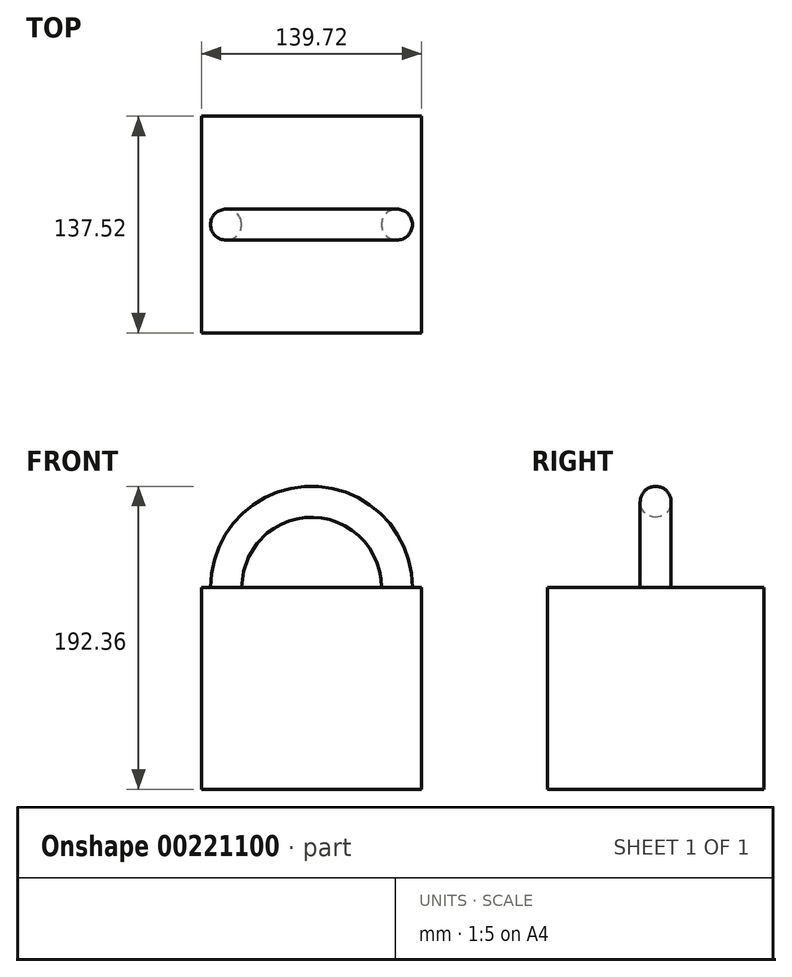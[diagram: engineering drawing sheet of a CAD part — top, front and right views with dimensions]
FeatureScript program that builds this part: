
annotation { "Feature Type Name" : "Feature", "Feature Type Description" : "" }
export const myFeature = defineFeature(function(context is Context, id is Id, definition is map)
    precondition{}
    {
        {
            var Q0;
            Q0=qCreatedBy(makeId("Top.planeOp"),FACE);
            var sketch = newSketch(context, id + "F0", { "sketchPlane" : qUnion([Q0])});
            skLineSegment(sketch, "E0.bottom", {"start": v(69.86, -68.76) * mm, "end": v(-69.86, -68.76) * mm});
            skLineSegment(sketch, "E0.top", {"start": v(69.86, 68.76) * mm, "end": v(-69.86, 68.76) * mm});
            skLineSegment(sketch, "E0.left", {"start": v(69.86, -68.76) * mm, "end": v(69.86, 68.76) * mm});
            skLineSegment(sketch, "E0.right", {"start": v(-69.86, -68.76) * mm, "end": v(-69.86, 68.76) * mm});
            skPoint(sketch, "E0.middle", {"position": v(0, 0) * mm});
            skLineSegment(sketch, "E1", {"start": v(0, 68.76) * mm, "end": v(0, -68.76) * mm});
            skSolve(sketch);
        }
        {
            var Q0;
            Q0=qCreatedBy(makeId("Top.planeOp"),FACE);
            var sketch = newSketch(context, id + "F1", { "sketchPlane" : qUnion([Q0])});
            skCircle(sketch, "E2", {"center": v(54.26, 0) * mm, "radius": 9.82 * mm});
            skSolve(sketch);
        }
        {
            var Q0;
            Q0=makeQuery(id+"F1.imprint","IMPRINT",FACE,{"disambiguationData":[TD([[makeQuery(id+"F1.imprint","IMPRINT",EDGE,{"derivedFrom":sQuery(id+"F1.wireOp",EDGE,"E2")}),1.0]])]});
            var Q1;
            Q1=sQuery(id+"F0.wireOp",EDGE,"E1");
            revolve(context, id + "F2", {"entities" : qUnion([Q0]), "axis" : qUnion([Q1]), "revolveType" : RevolveType.FULL});
        }
        {
            var Q0;
            {var subQ0=sQuery(id+"F0.wireOp",EDGE,"E0.right");Q0=makeQuery(id+"F0.imprint","IMPRINT",FACE,{"disambiguationData":[TD([[makeQuery(id+"F0.imprint","IMPRINT",EDGE,{"derivedFrom":subQ0}),-1.0]])]});}
            var Q1;
            {var subQ0=sQuery(id+"F0.wireOp",EDGE,"E0.left");Q1=makeQuery(id+"F0.imprint","IMPRINT",FACE,{"disambiguationData":[TD([[makeQuery(id+"F0.imprint","IMPRINT",EDGE,{"derivedFrom":subQ0}),1.0]])]});}
            extrude(context, id + "F3", {"entities" : qUnion([Q0, Q1]), "operationType" : NewBodyOperationType.ADD, "oppositeDirection" : true, "depth" : 128.27 * mm});
        }
    });
